# Revit family: Haworth_Immerse_ShiftTable_RectangleRound
name_source: partatom
category: Furniture Systems
revit_build: Autodesk Revit 2018 (Build: 20170223_1515(x64)
units: mm (PartAtom-declared; Revit-internal decimal feet)

## family parameters
Always vertical = Yes
Cut with Voids When Loaded = No
OmniClass Number = 23.40.70.14.64.21
OmniClass Title = Systems Furniture
Part Type = Normal
Room Calculation Point = No
Round Connector Dimension = Use Diameter
Shared = No
Work Plane-Based = No

## types (4) — shared parameters
Actual Depth = 60"
Actual Height = 29"
Actual Width = 138"
Assembly Code = E2020200
Manufacturer = Haworth
Model = THRD-48D8
Revision Number = 1
Size = Verify Final Dim. w/ Haworth
Standard Height = 29 in.
Standard Size = 48d 96w, 60d 60w
URL = https://www.haworth.com
URL - Product = http://www.haworth.com
Void Baseline Height = 18"
Warranty = http://www.haworth.com

## per-type parameters (varying)
| type | Description | Oblong Planter | Oblong Planter Void Height | Round Planter | Round Planter Void Height |
| 48d 96w 60dia 29h - Round Planter | Haworth Immerse Shift Table Rectangle Round - 448d 96w 60dia 29h - Round Planter | No | 6" | Yes | 30" |
| 48d 96w 60dia 29h - No Planter | Haworth Immerse Shift Table Rectangle Round - 48d 96w 60dia 29h - No Planters | No | 6" | No | 6" |
| 48d 96w 60dia 29h - Oblong Planter | Haworth Immerse Shift Table Rectangle Round - 48d 96w 60dia 29h - Oblong Planter | Yes | 22" | No | 6" |
| 48d 96w 60dia 29h - Two Planters | Haworth Immerse Shift Table Rectangle Round - 48d 96w 60dia 29h - Two Planters | Yes | 22" | Yes | 30" |

## geometry (parser evidence)
native form markers: Sweep x8
no freeform markers — native parametric forms only
